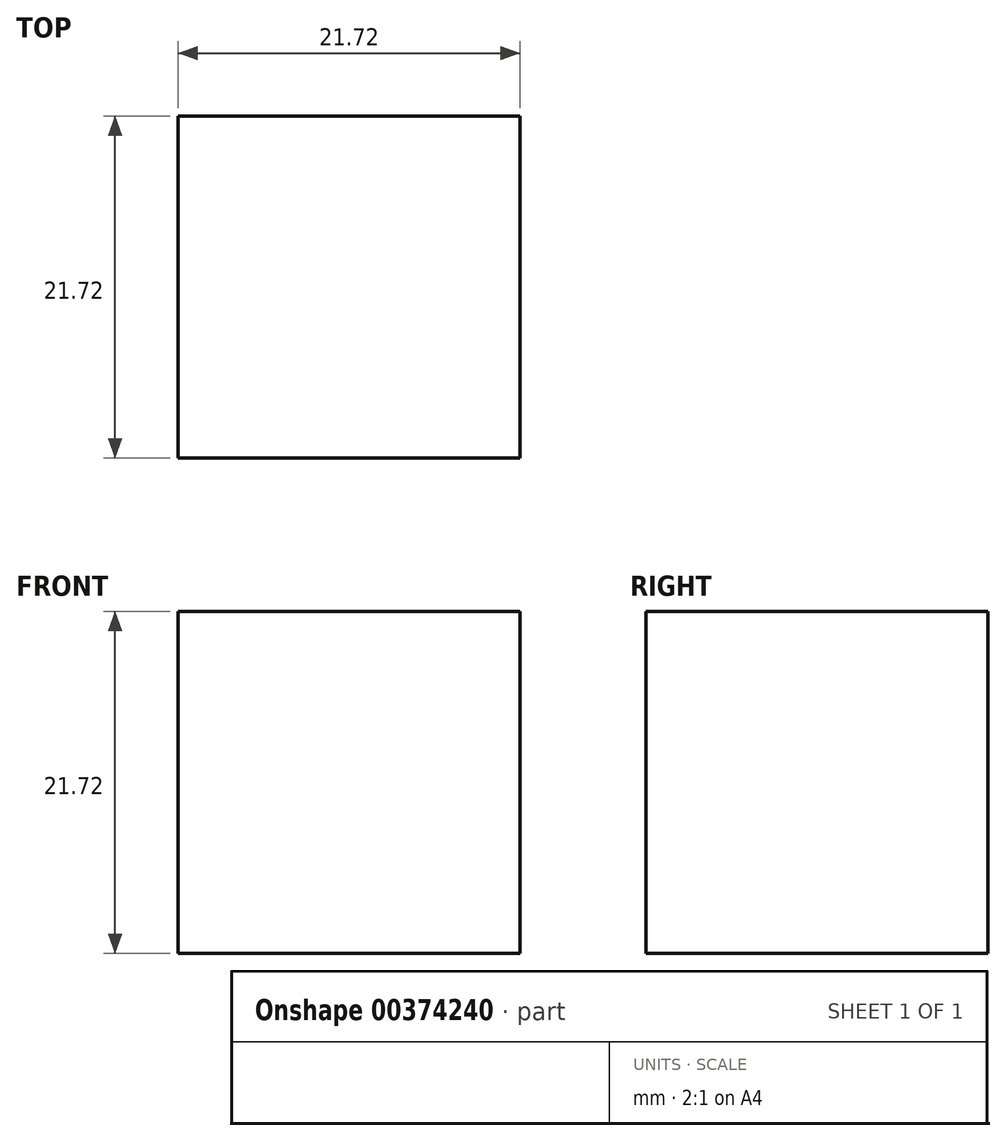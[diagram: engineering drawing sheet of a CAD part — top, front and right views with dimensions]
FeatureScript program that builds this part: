
annotation { "Feature Type Name" : "Feature", "Feature Type Description" : "" }
export const myFeature = defineFeature(function(context is Context, id is Id, definition is map)
    precondition{}
    {
        {
            var Q0;
            Q0=qCreatedBy(makeId("Top.planeOp"),FACE);
            var sketch = newSketch(context, id + "F0", { "sketchPlane" : qUnion([Q0])});
            skLineSegment(sketch, "E0.bottom", {"start": v(-4.26, -5.82) * mm, "end": v(17.46, -5.82) * mm});
            skLineSegment(sketch, "E0.top", {"start": v(-4.26, -27.54) * mm, "end": v(17.46, -27.54) * mm});
            skLineSegment(sketch, "E0.left", {"start": v(-4.26, -5.82) * mm, "end": v(-4.26, -27.54) * mm});
            skLineSegment(sketch, "E0.right", {"start": v(17.46, -5.82) * mm, "end": v(17.46, -27.54) * mm});
            skSolve(sketch);
        }
        {
            var Q0;
            Q0=makeQuery(id+"F0.imprint","IMPRINT",FACE,{"disambiguationData":[TD([[makeQuery(id+"F0.imprint","IMPRINT",EDGE,{"derivedFrom":sQuery(id+"F0.wireOp",EDGE,"E0.bottom")}),-1.0]])]});
            extrude(context, id + "F1", {"entities" : qUnion([Q0]), "depth" : 21.72 * mm});
        }
    });
